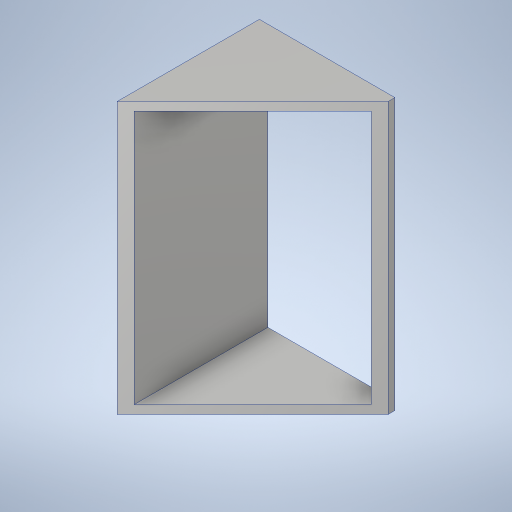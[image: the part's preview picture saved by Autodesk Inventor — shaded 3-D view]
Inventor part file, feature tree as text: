
AUTODESK INVENTOR PART (.ipt)
format: ipt  version: 2023.4 (Build 274418000, 418)  size: 240,128 bytes
history: native  units: in
note: dims shown in document units (in); Inventor stores cm internally (conversion verified against a paired STEP export)
features: extrude x2, sketch x1
ambient origin geometry x8: Origin, YZ Plane, XZ Plane, XY Plane, X Axis, Y Axis, Z Axis, Center Point
bodies: Solid1 (feature_tree)
feature tree (3):
  extrude  "Extrusion1"  TaperAngle=45.0deg  [1 undecoded]
  extrude  "Extrusion2"  TaperAngle=0.0deg  [1 undecoded]
  sketch  "Sketch2"  dims[d4=0.0in d5=45.0deg d6=0.0in d7=0.0in]
note: 2 required parameter values undecoded (feature->parameter linkage not recoverable at this tier; creation-order binding heuristic only, values carry confidence <= 0.55)
